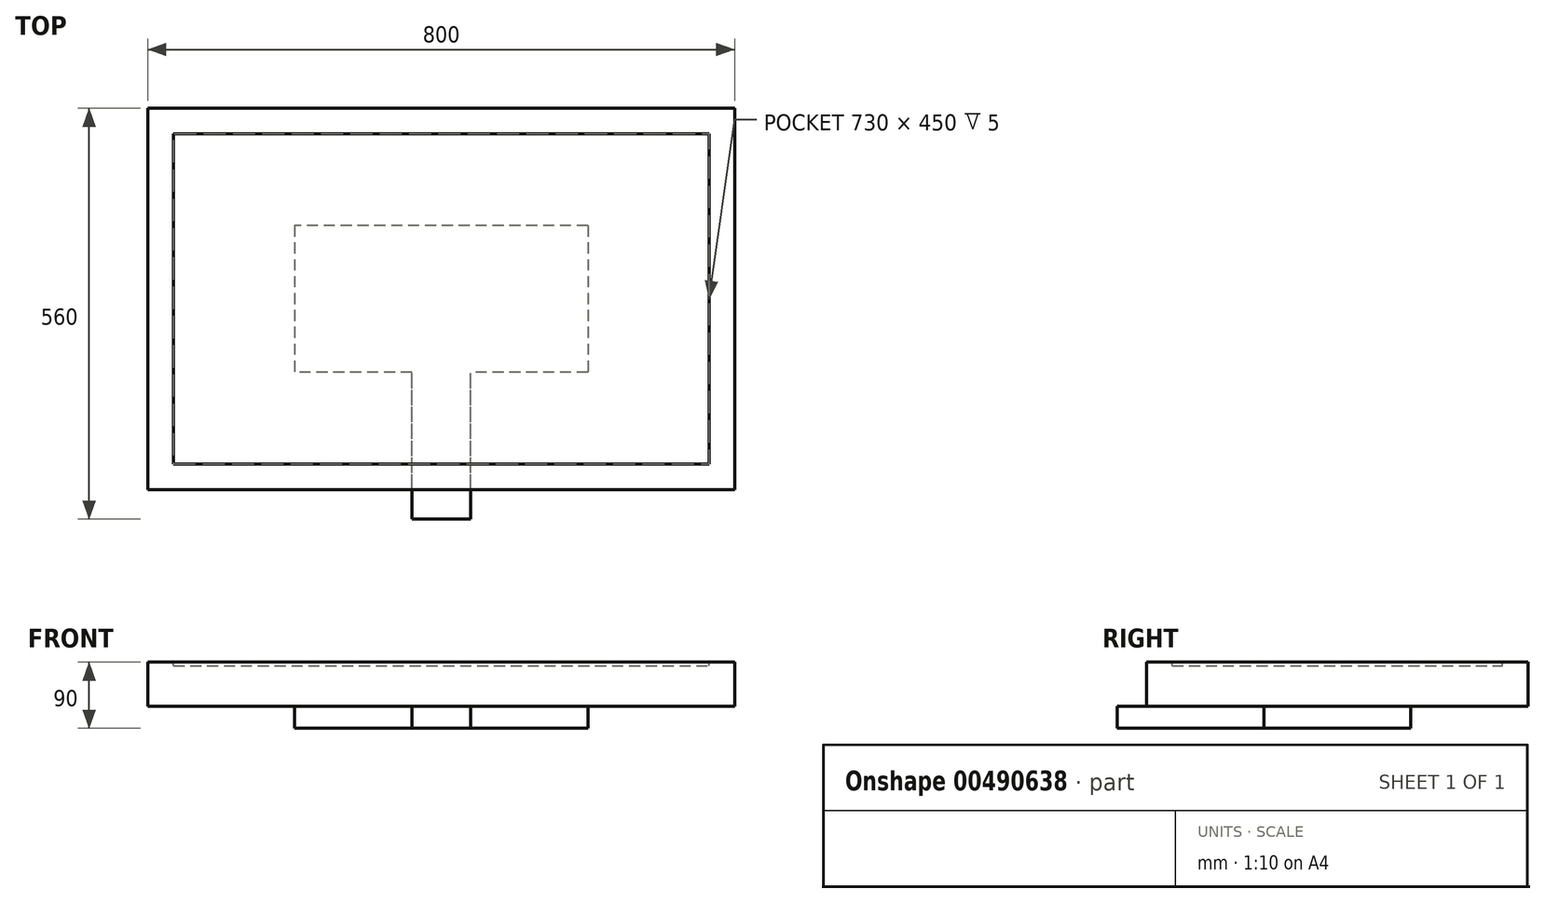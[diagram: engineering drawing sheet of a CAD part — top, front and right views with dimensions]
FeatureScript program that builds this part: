
annotation { "Feature Type Name" : "Feature", "Feature Type Description" : "" }
export const myFeature = defineFeature(function(context is Context, id is Id, definition is map)
    precondition{}
    {
        {
            var Q0;
            Q0=qCreatedBy(makeId("Top.planeOp"),FACE);
            var sketch = newSketch(context, id + "F0", { "sketchPlane" : qUnion([Q0])});
            skLineSegment(sketch, "E0.bottom", {"start": v(0, 0) * mm, "end": v(-800, 0) * mm});
            skLineSegment(sketch, "E0.top", {"start": v(0, -520) * mm, "end": v(-800, -520) * mm});
            skLineSegment(sketch, "E0.left", {"start": v(0, 0) * mm, "end": v(0, -520) * mm});
            skLineSegment(sketch, "E0.right", {"start": v(-800, 0) * mm, "end": v(-800, -520) * mm});
            skSolve(sketch);
        }
        {
            var Q0;
            Q0=makeQuery(id+"F0.imprint","IMPRINT",FACE,{"disambiguationData":[TD([[makeQuery(id+"F0.imprint","IMPRINT",EDGE,{"derivedFrom":sQuery(id+"F0.wireOp",EDGE,"E0.bottom")}),1.0]])]});
            extrude(context, id + "F1", {"entities" : qUnion([Q0]), "depth" : 60 * mm});
        }
        {
            var Q0;
            Q0=makeQuery(id+"F1.opExtrude","CAP_FACE",FACE,{"disambiguationData":[OSD([sQuery(id+"F0.wireOp",EDGE,"E0.bottom"),sQuery(id+"F0.wireOp",EDGE,"E0.top"),sQuery(id+"F0.wireOp",EDGE,"E0.left"),sQuery(id+"F0.wireOp",EDGE,"E0.right")])],"isStart":true});
            var sketch = newSketch(context, id + "F2", { "sketchPlane" : qUnion([Q0])});
            skLineSegment(sketch, "E1.bottom", {"start": v(-200, 160) * mm, "end": v(-600, 160) * mm});
            skLineSegment(sketch, "E1.top", {"start": v(-200, 360) * mm, "end": v(-600, 360) * mm});
            skLineSegment(sketch, "E1.left", {"start": v(-200, 160) * mm, "end": v(-200, 360) * mm});
            skLineSegment(sketch, "E1.right", {"start": v(-600, 160) * mm, "end": v(-600, 360) * mm});
            skSolve(sketch);
        }
        {
            var Q0;
            Q0=makeQuery(id+"F2.imprint","IMPRINT",FACE,{"disambiguationData":[TD([[makeQuery(id+"F2.imprint","IMPRINT",EDGE,{"derivedFrom":sQuery(id+"F2.wireOp",EDGE,"E1.bottom")}),-1.0]])]});
            extrude(context, id + "F3", {"entities" : qUnion([Q0]), "operationType" : NewBodyOperationType.ADD, "depth" : 30 * mm});
        }
        {
            var Q0;
            Q0=makeQuery(id+"F3.opExtrude","SWEPT_FACE",FACE,{"disambiguationData":[OSD([sQuery(id+"F2.wireOp",EDGE,"E1.top")])]});
            var sketch = newSketch(context, id + "F4", { "sketchPlane" : qUnion([Q0])});
            skLineSegment(sketch, "E2.bottom", {"start": v(-360, 0) * mm, "end": v(-440, 0) * mm});
            skLineSegment(sketch, "E2.top", {"start": v(-360, -30) * mm, "end": v(-440, -30) * mm});
            skLineSegment(sketch, "E2.left", {"start": v(-360, 0) * mm, "end": v(-360, -30) * mm});
            skLineSegment(sketch, "E2.right", {"start": v(-440, 0) * mm, "end": v(-440, -30) * mm});
            skSolve(sketch);
        }
        {
            var Q0;
            Q0=makeQuery(id+"F4.imprint","IMPRINT",FACE,{"disambiguationData":[TD([[makeQuery(id+"F4.imprint","IMPRINT",EDGE,{"derivedFrom":sQuery(id+"F4.wireOp",EDGE,"E2.bottom")}),1.0]])]});
            var Q1;
            Q1=makeQuery(id+"F1.opExtrude","SWEPT_FACE",FACE,{"disambiguationData":[OSD([sQuery(id+"F0.wireOp",EDGE,"E0.top")])]});
            extrude(context, id + "F5", {"entities" : qUnion([Q0]), "operationType" : NewBodyOperationType.ADD, "endBoundEntityFace" : qUnion([Q1]), "depth" : 200 * mm});
        }
        {
            var Q0;
            Q0=makeQuery(id+"F1.opExtrude","CAP_FACE",FACE,{"disambiguationData":[OSD([sQuery(id+"F0.wireOp",EDGE,"E0.bottom"),sQuery(id+"F0.wireOp",EDGE,"E0.top"),sQuery(id+"F0.wireOp",EDGE,"E0.left"),sQuery(id+"F0.wireOp",EDGE,"E0.right")])],"isStart":false});
            var sketch = newSketch(context, id + "F6", { "sketchPlane" : qUnion([Q0])});
            skLineSegment(sketch, "E3.bottom", {"start": v(-765, -485) * mm, "end": v(-35, -485) * mm});
            skLineSegment(sketch, "E3.top", {"start": v(-765, -35) * mm, "end": v(-35, -35) * mm});
            skLineSegment(sketch, "E3.left", {"start": v(-765, -485) * mm, "end": v(-765, -35) * mm});
            skLineSegment(sketch, "E3.right", {"start": v(-35, -485) * mm, "end": v(-35, -35) * mm});
            skSolve(sketch);
        }
        {
            var Q0;
            Q0 = qSketchRegion(id + "F6", true);
            extrude(context, id + "F7", {"entities" : qUnion([Q0]), "operationType" : NewBodyOperationType.REMOVE, "oppositeDirection" : true, "depth" : 5 * mm});
        }
    });
